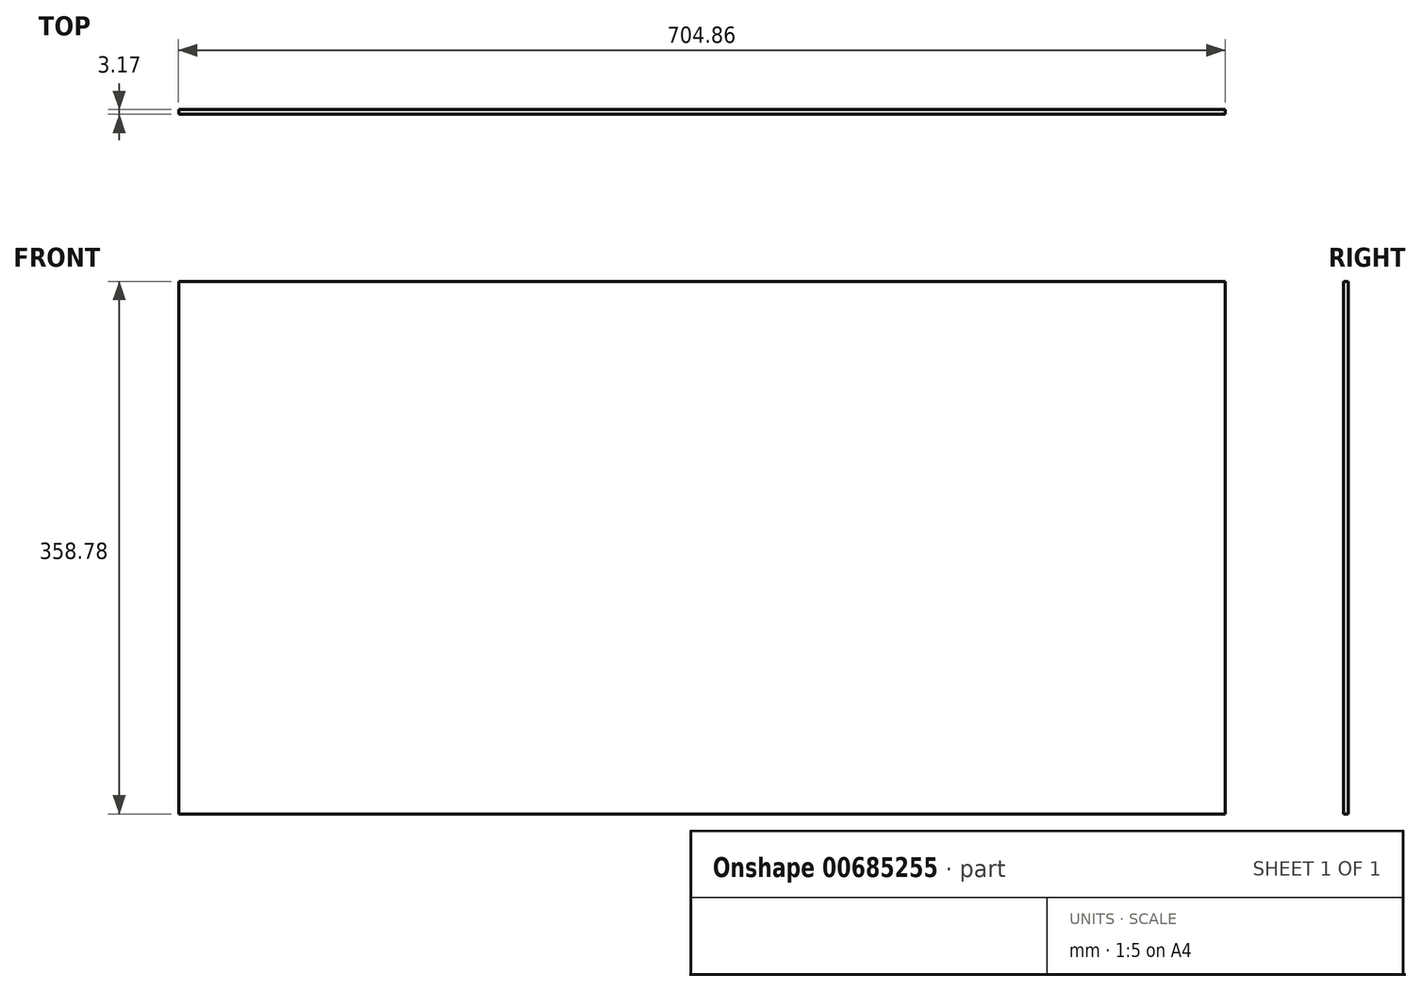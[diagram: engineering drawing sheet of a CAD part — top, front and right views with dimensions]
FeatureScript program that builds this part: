
annotation { "Feature Type Name" : "Feature", "Feature Type Description" : "" }
export const myFeature = defineFeature(function(context is Context, id is Id, definition is map)
    precondition{}
    {
        {
            var Q0;
            Q0=qCreatedBy(makeId("Front.planeOp"),FACE);
            var sketch = newSketch(context, id + "F0", { "sketchPlane" : qUnion([Q0])});
            skLineSegment(sketch, "E0.bottom", {"start": v(352.43, 179.39) * mm, "end": v(-352.43, 179.39) * mm});
            skLineSegment(sketch, "E0.top", {"start": v(352.43, -179.39) * mm, "end": v(-352.43, -179.39) * mm});
            skLineSegment(sketch, "E0.left", {"start": v(352.43, 179.39) * mm, "end": v(352.43, -179.39) * mm});
            skLineSegment(sketch, "E0.right", {"start": v(-352.43, 179.39) * mm, "end": v(-352.43, -179.39) * mm});
            skPoint(sketch, "E0.middle", {"position": v(0, 0) * mm});
            skSolve(sketch);
        }
        {
            var Q0;
            Q0=qSketchRegion(id+"F0",true);
            extrude(context, id + "F1", {"entities" : qUnion([Q0]), "depth" : 3.17 * mm, "offsetDistance" : 25.4 * mm});
        }
    });
